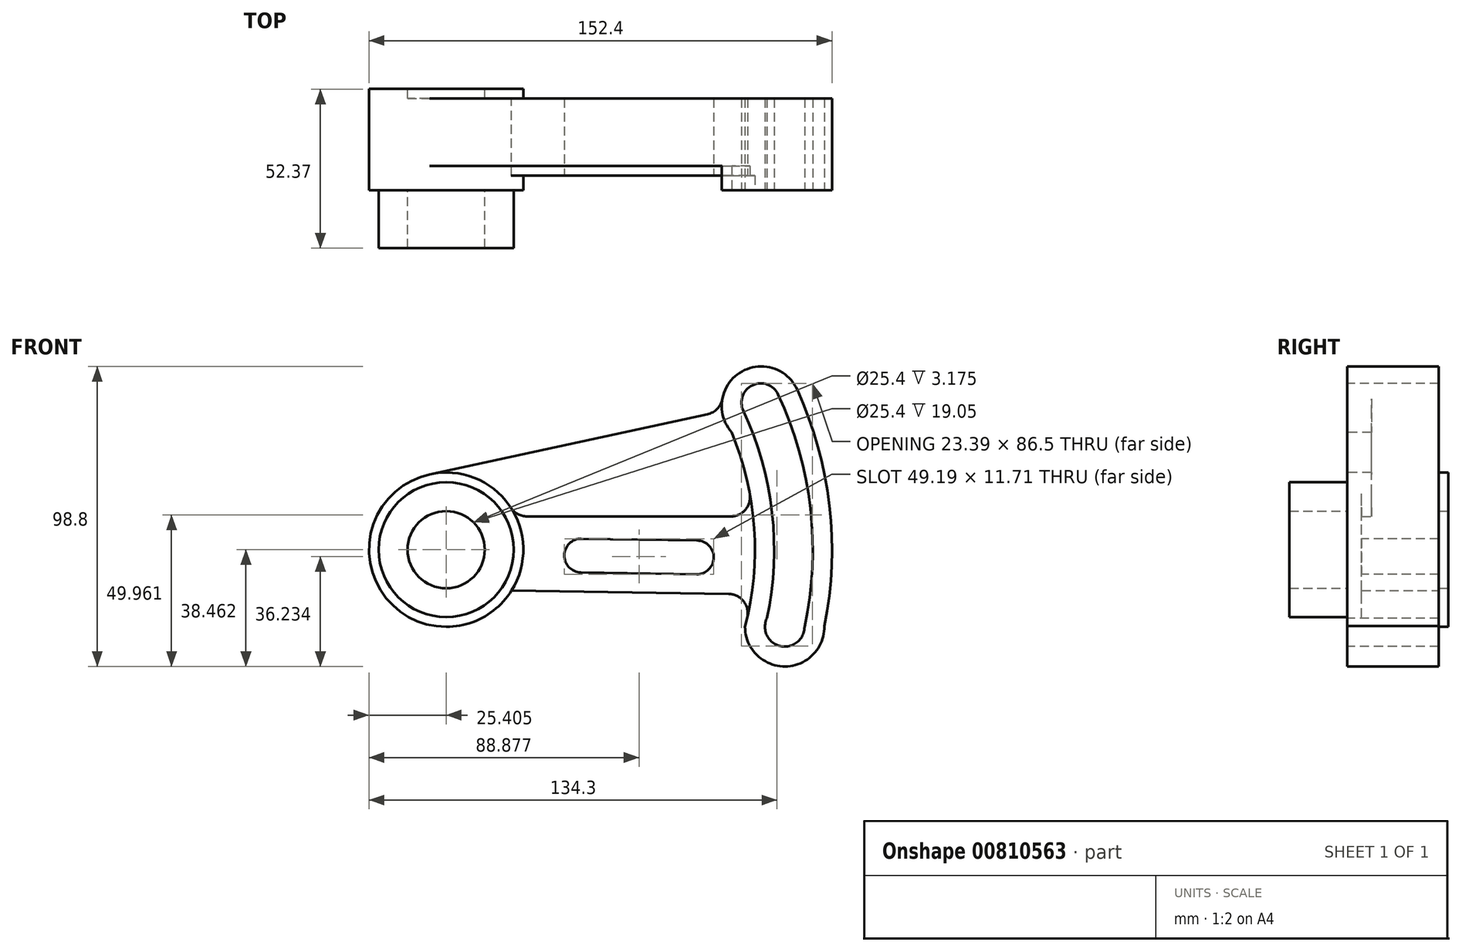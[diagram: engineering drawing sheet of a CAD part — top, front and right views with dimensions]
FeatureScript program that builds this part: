
annotation { "Feature Type Name" : "Feature", "Feature Type Description" : "" }
export const myFeature = defineFeature(function(context is Context, id is Id, definition is map)
    precondition{}
    {
        {
            var Q0;
            Q0=qCreatedBy(makeId("Front.planeOp"),FACE);
            var sketch = newSketch(context, id + "F0", { "sketchPlane" : qUnion([Q0])});
            skCircle(sketch, "E0", {"center": v(-55.82, -6.35) * mm, "radius": 12.7 * mm});
            skSolve(sketch);
        }
        {
            var Q0;
            Q0=makeQuery(id+"F0.imprint","IMPRINT",FACE,{"disambiguationData":[TD([[makeQuery(id+"F0.imprint","IMPRINT",EDGE,{"derivedFrom":sQuery(id+"F0.wireOp",EDGE,"E0")}),1.0]])]});
            var sketch = newSketch(context, id + "F1", { "sketchPlane" : qUnion([Q0])});
            skCircle(sketch, "E1", {"center": v(-55.82, -6.35) * mm, "radius": 22.23 * mm});
            skSolve(sketch);
        }
        {
            var Q0;
            Q0=makeQuery(id+"F1.imprint","IMPRINT",FACE,{"disambiguationData":[TD([[makeQuery(id+"F1.imprint","IMPRINT",EDGE,{"derivedFrom":sQuery(id+"F1.wireOp",EDGE,"E1")}),1.0]])]});
            var sketch = newSketch(context, id + "F2", { "sketchPlane" : qUnion([Q0])});
            skCircle(sketch, "E2", {"center": v(-55.82, -6.35) * mm, "radius": 25.4 * mm});
            skSolve(sketch);
        }
        {
            var Q0;
            Q0=makeQuery(id+"F1.imprint","IMPRINT",FACE,{"disambiguationData":[TD([[makeQuery(id+"F1.imprint","IMPRINT",EDGE,{"derivedFrom":sQuery(id+"F1.wireOp",EDGE,"E1")}),1.0]])]});
            extrude(context, id + "F3", {"entities" : qUnion([Q0]), "depth" : 19.05 * mm, "offsetDistance" : 25.4 * mm});
        }
        {
            var Q0;
            Q0=makeQuery(id+"F2.imprint","IMPRINT",FACE,{"disambiguationData":[TD([[makeQuery(id+"F2.imprint","IMPRINT",EDGE,{"derivedFrom":makeQuery(id+"F1.imprint","IMPRINT",EDGE,{"derivedFrom":sQuery(id+"F1.wireOp",EDGE,"E1")})}),1.0]])]});
            var Q1;
            Q1=makeQuery(id+"F2.imprint","IMPRINT",FACE,{"disambiguationData":[TD([[makeQuery(id+"F2.imprint","IMPRINT",EDGE,{"derivedFrom":sQuery(id+"F2.wireOp",EDGE,"E2")}),1.0]])]});
            extrude(context, id + "F4", {"entities" : qUnion([Q0, Q1]), "operationType" : NewBodyOperationType.ADD, "oppositeDirection" : true, "depth" : 33.32 * mm, "offsetDistance" : 25.4 * mm});
        }
        {
            var Q0;
            Q0=makeQuery(id+"F2.imprint","IMPRINT",FACE,{"disambiguationData":[TD([[makeQuery(id+"F2.imprint","IMPRINT",EDGE,{"derivedFrom":makeQuery(id+"F1.imprint","IMPRINT",EDGE,{"derivedFrom":makeQuery(id+"F0.imprint","IMPRINT",EDGE,{"derivedFrom":sQuery(id+"F0.wireOp",EDGE,"E0")})})}),1.0]])]});
            var sketch = newSketch(context, id + "F5", { "sketchPlane" : qUnion([Q0])});
            skLineSegment(sketch, "E3", {"start": v(-55.82, -6.35) * mm, "end": v(-30.42, -6.35) * mm});
            skLineSegment(sketch, "E4", {"start": v(-61.19, 18.48) * mm, "end": v(34.96, 39.3) * mm});
            skArc(sketch, "E5", {"start": v(38.14, 32.3) * mm, "mid": v(45.54, 0.64) * mm, "end": v(42.56, -31.75) * mm});
            skLineSegment(sketch, "E6", {"start": v(-32.9, 4.6) * mm, "end": v(45.2, 4.6) * mm});
            skLineSegment(sketch, "E7", {"start": v(44.71, -21.07) * mm, "end": v(-34.27, -19.8) * mm});
            skArc(sketch, "E8", {"start": v(41.98, 39.37) * mm, "mid": v(51.6, 4.42) * mm, "end": v(49.1, -31.75) * mm});
            skArc(sketch, "E9", {"start": v(59.72, 46.38) * mm, "mid": v(70.35, 8.16) * mm, "end": v(68.67, -31.47) * mm});
            skArc(sketch, "E10", {"start": v(53.48, 44.75) * mm, "mid": v(64.07, 7.2) * mm, "end": v(62.13, -31.75) * mm});
            skLineSegment(sketch, "E11", {"start": v(28.44, -31.75) * mm, "end": v(42.56, -31.75) * mm});
            skLineSegment(sketch, "E12", {"start": v(49.1, -31.75) * mm, "end": v(62.13, -31.75) * mm});
            skLineSegment(sketch, "E13", {"start": v(62.13, -31.75) * mm, "end": v(62.13, -31.75) * mm});
            skLineSegment(sketch, "E14", {"start": v(68.68, -31.75) * mm, "end": v(86.23, -31.75) * mm});
            skArc(sketch, "E15", {"start": v(53.48, 44.75) * mm, "mid": v(45.04, 47.8) * mm, "end": v(41.98, 39.37) * mm});
            skArc(sketch, "E16", {"start": v(49.75, -28.93) * mm, "mid": v(54.17, -38.1) * mm, "end": v(62.13, -31.74) * mm});
            skPoint(sketch, "E17.orphan", {"position": v(58.48, -6.35) * mm});
            skArc(sketch, "E18", {"start": v(59.72, 46.38) * mm, "mid": v(40.76, 51.88) * mm, "end": v(38.14, 32.3) * mm});
            skArc(sketch, "E19", {"start": v(42.56, -31.75) * mm, "mid": v(55.76, -44.8) * mm, "end": v(68.67, -31.47) * mm});
            skLineSegment(sketch, "E20", {"start": v(59.72, 46.38) * mm, "end": v(59.72, 46.38) * mm});
            skLineSegment(sketch, "E21", {"start": v(34.96, 39.3) * mm, "end": v(62.67, 45.3) * mm});
            skArc(sketch, "E22.converted", {"start": v(-61.19, 18.48) * mm, "mid": v(-67, -29.15) * mm, "end": v(-32.9, 4.6) * mm});
            skCircle(sketch, "E23", {"center": v(-55.82, -6.35) * mm, "radius": 25.4 * mm});
            skSolve(sketch);
        }
        {
            var Q0;
            Q0 = qSketchRegion(id + "F5", true);
            extrude(context, id + "F6", {"entities" : qUnion([Q0]), "operationType" : NewBodyOperationType.ADD, "oppositeDirection" : true, "depth" : 30.15 * mm, "offsetDistance" : 25.4 * mm});
        }
        {
            var Q0;
            {var subQ1=sQuery(id+"F5.wireOp",EDGE,"E4");Q0=makeQuery(id+"F5.imprint","IMPRINT",FACE,{"disambiguationData":[TD([[makeQuery(id+"F5.imprint","IMPRINT",EDGE,{"derivedFrom":subQ1}),-1.0]])]});}
            var Q1;
            {var subQ2=sQuery(id+"F5.wireOp",EDGE,"E6");Q1=makeQuery(id+"F5.imprint","IMPRINT",FACE,{"disambiguationData":[TD([[makeQuery(id+"F5.imprint","IMPRINT",EDGE,{"derivedFrom":subQ2}),-1.0]])]});}
            var Q2;
            {var subQ16=sQuery(id+"F5.wireOp",EDGE,"E18");var subQ17=sQuery(id+"F5.wireOp",EDGE,"E5");var subQ18=makeQuery(id+"F5.imprint","INTERSECT",VERTEX,{"derivedFrom":[subQ17,subQ16]});Q2=makeQuery(id+"F5.imprint","IMPRINT",FACE,{"disambiguationData":[TD([[makeQuery(id+"F5.imprint","IMPRINT",EDGE,{"disambiguationData":[TD([[subQ18,-1.0]])],"derivedFrom":subQ17}),1.0]])]});}
            var Q3;
            {var subQ1=sQuery(id+"F5.wireOp",EDGE,"E18");var subQ3=sQuery(id+"F5.wireOp",EDGE,"E9");var subQ4=makeQuery(id+"F5.imprint","INTERSECT",VERTEX,{"derivedFrom":[subQ3,subQ1]});Q3=makeQuery(id+"F5.imprint","IMPRINT",FACE,{"disambiguationData":[TD([[makeQuery(id+"F5.imprint","IMPRINT",EDGE,{"disambiguationData":[TD([[subQ4,-1.0]])],"derivedFrom":subQ3}),-1.0]])]});}
            extrude(context, id + "F7", {"entities" : qUnion([Q0, Q1, Q2, Q3]), "operationType" : NewBodyOperationType.REMOVE, "oppositeDirection" : true, "depth" : 4.75 * mm, "offsetDistance" : 25.4 * mm});
        }
        {
            var Q0;
            {var subQ2=sQuery(id+"F5.wireOp",EDGE,"E4");Q0=makeQuery(id+"F5.imprint","IMPRINT",FACE,{"disambiguationData":[TD([[makeQuery(id+"F5.imprint","IMPRINT",EDGE,{"derivedFrom":subQ2}),-1.0]])]});}
            extrude(context, id + "F8", {"entities" : qUnion([Q0]), "operationType" : NewBodyOperationType.REMOVE, "oppositeDirection" : true, "depth" : 7.94 * mm, "offsetDistance" : 25.4 * mm});
        }
        {
            var Q0;
            Q0=makeQuery(id+"F7.boolean.opBoolean","COPY",FACE,{"derivedFrom":makeQuery(id+"F7.opExtrude","CAP_FACE",FACE,{"disambiguationData":[OSD([sQuery(id+"F5.wireOp",EDGE,"E4"),sQuery(id+"F5.wireOp",EDGE,"E5"),sQuery(id+"F5.wireOp",EDGE,"E7"),sQuery(id+"F5.wireOp",EDGE,"E8"),sQuery(id+"F5.wireOp",EDGE,"E9"),sQuery(id+"F5.wireOp",EDGE,"E10"),sQuery(id+"F5.wireOp",EDGE,"E15"),sQuery(id+"F5.wireOp",EDGE,"E16"),sQuery(id+"F5.wireOp",EDGE,"E18"),sQuery(id+"F5.wireOp",EDGE,"E19"),sQuery(id+"F5.wireOp",EDGE,"E23")])],"isStart":false})});
            var sketch = newSketch(context, id + "F9", { "sketchPlane" : qUnion([Q0])});
            skLineSegment(sketch, "E24.bottom", {"start": v(-11.48, -13.82) * mm, "end": v(26.62, -14.43) * mm});
            skLineSegment(sketch, "E24.top", {"start": v(-11.3, -2.72) * mm, "end": v(26.8, -3.33) * mm});
            skArc(sketch, "E25", {"start": v(-11.3, -2.72) * mm, "mid": v(-16.94, -8.18) * mm, "end": v(-11.48, -13.82) * mm});
            skArc(sketch, "E26", {"start": v(26.62, -14.43) * mm, "mid": v(32.25, -8.97) * mm, "end": v(26.8, -3.33) * mm});
            skSolve(sketch);
        }
        {
            var Q0;
            Q0 = qSketchRegion(id + "F9", true);
            extrude(context, id + "F10", {"entities" : qUnion([Q0]), "operationType" : NewBodyOperationType.REMOVE, "oppositeDirection" : true, "depth" : 25.4 * mm, "offsetDistance" : 25.4 * mm});
        }
        {
            var Q0;
            Q0=makeQuery(id+"F7.boolean.opBoolean","SPLIT",EDGE,{"derivedFrom":makeQuery(id+"F6.opExtrude","SWEPT_EDGE",EDGE,{"disambiguationData":[OSD([sQuery(id+"F5.wireOp",EDGE,"E7"),sQuery(id+"F5.wireOp",EDGE,"E23")])]})});
            var Q1;
            Q1=makeQuery(id+"F8.boolean.opBoolean","COPY",EDGE,{"derivedFrom":makeQuery(id+"F8.opExtrude","SWEPT_EDGE",EDGE,{"disambiguationData":[OSD([sQuery(id+"F5.wireOp",EDGE,"E6"),sQuery(id+"F5.wireOp",EDGE,"E23")])]})});
            var Q2;
            Q2=makeQuery(id+"F6.opExtrude","SWEPT_EDGE",EDGE,{"disambiguationData":[OSD([sQuery(id+"F5.wireOp",EDGE,"E4"),sQuery(id+"F5.wireOp",EDGE,"E18"),sQuery(id+"F5.wireOp",EDGE,"E21")])]});
            var Q3;
            Q3=makeQuery(id+"F8.boolean.opBoolean","COPY",EDGE,{"derivedFrom":makeQuery(id+"F8.opExtrude","SWEPT_EDGE",EDGE,{"disambiguationData":[OSD([sQuery(id+"F5.wireOp",EDGE,"E5"),sQuery(id+"F5.wireOp",EDGE,"E6")])]})});
            var Q4;
            Q4=makeQuery(id+"F6.opExtrude","SWEPT_EDGE",EDGE,{"disambiguationData":[OSD([sQuery(id+"F5.wireOp",EDGE,"E5"),sQuery(id+"F5.wireOp",EDGE,"E7")])]});
            fillet(context, id + "F11", {"entities" : qUnion([Q0, Q1, Q2, Q3, Q4]), "radius" : 6.35 * mm, "tangentPropagation" : true, "allowEdgeOverflow" : false});
        }
    });
